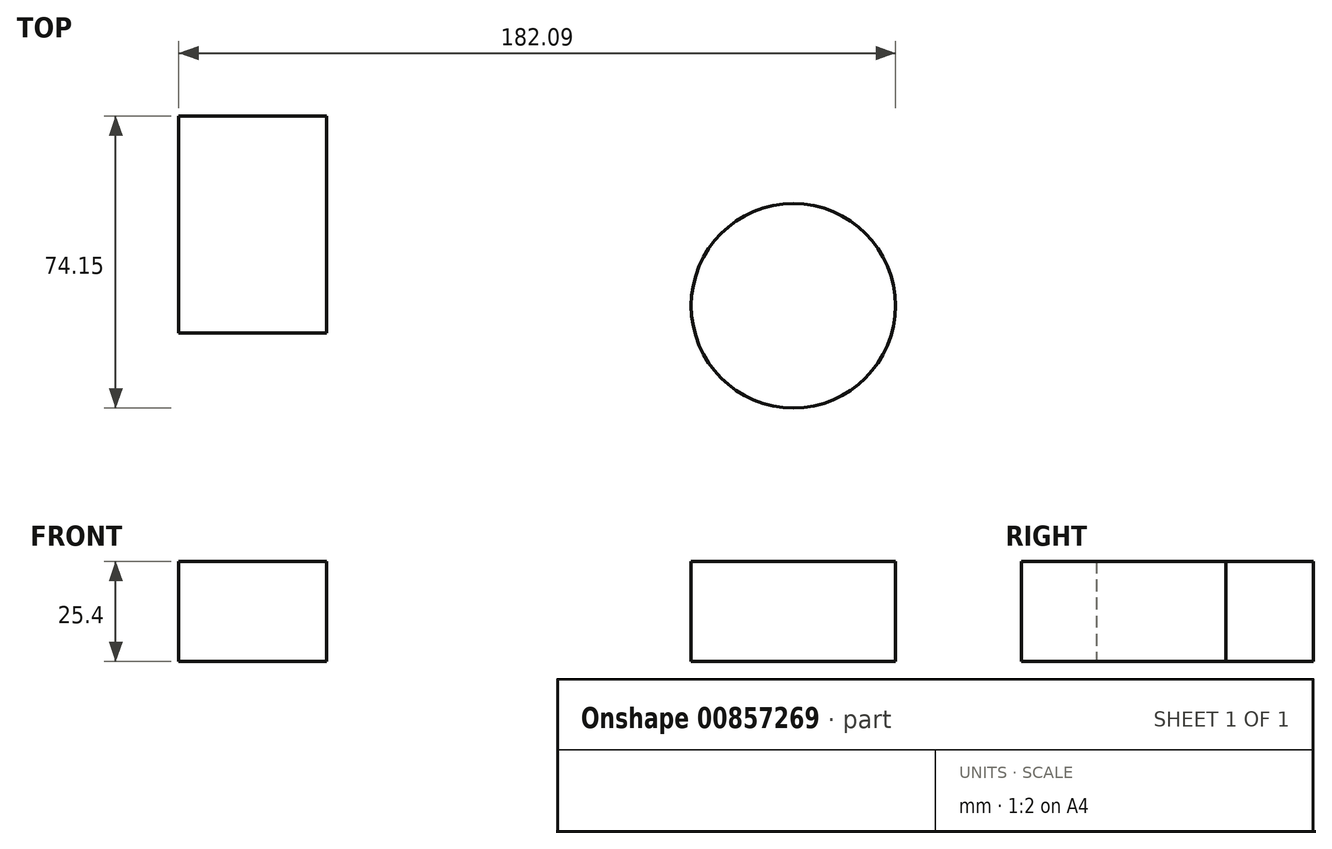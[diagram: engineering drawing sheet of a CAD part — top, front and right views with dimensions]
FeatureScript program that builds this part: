
annotation { "Feature Type Name" : "Feature", "Feature Type Description" : "" }
export const myFeature = defineFeature(function(context is Context, id is Id, definition is map)
    precondition{}
    {
        {
            var Q0;
            Q0=qCreatedBy(makeId("Top.planeOp"),FACE);
            var sketch = newSketch(context, id + "F0", { "sketchPlane" : qUnion([Q0])});
            skLineSegment(sketch, "E0.bottom", {"start": v(-123.38, 34.5) * mm, "end": v(-85.78, 34.5) * mm});
            skLineSegment(sketch, "E0.top", {"start": v(-123.38, -20.61) * mm, "end": v(-85.78, -20.61) * mm});
            skLineSegment(sketch, "E0.left", {"start": v(-123.38, 34.5) * mm, "end": v(-123.38, -20.61) * mm});
            skLineSegment(sketch, "E0.right", {"start": v(-85.78, 34.5) * mm, "end": v(-85.78, -20.61) * mm});
            skCircle(sketch, "E1", {"center": v(32.75, -13.69) * mm, "radius": 25.96 * mm});
            skSolve(sketch);
        }
        {
            var Q0;
            Q0 = qSketchRegion(id + "F0", true);
            extrude(context, id + "F1", {"entities" : qUnion([Q0]), "depth" : 25.4 * mm, "offsetDistance" : 25.4 * mm});
        }
    });
